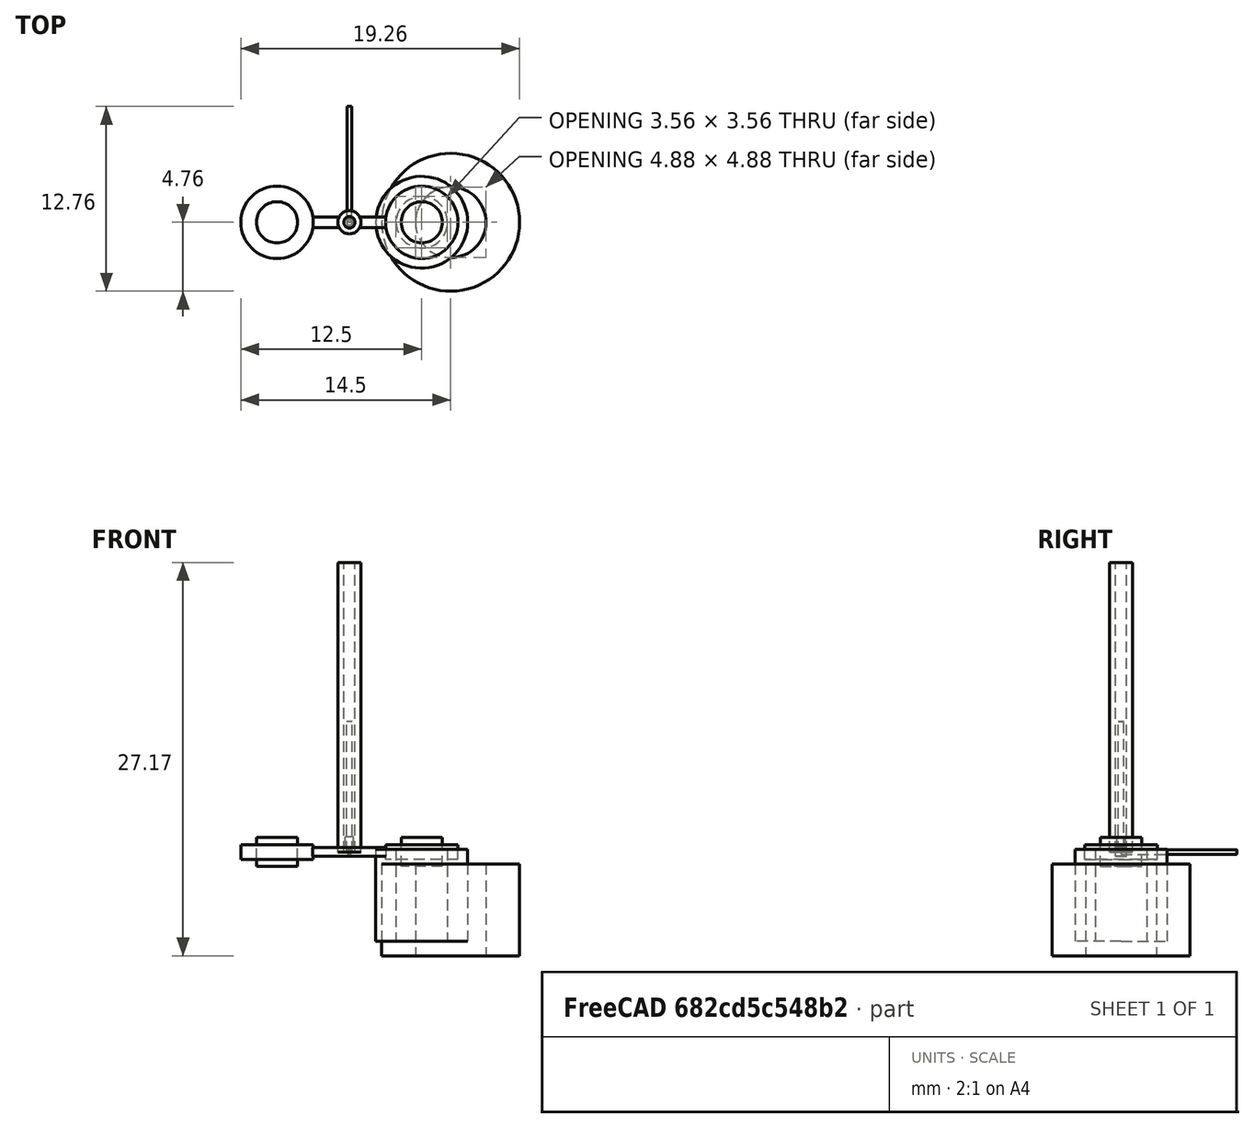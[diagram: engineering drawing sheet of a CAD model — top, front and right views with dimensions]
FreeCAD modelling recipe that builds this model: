
FCSTD DOCUMENT  (FreeCAD 0.18R15536 (Git))
Label: bowtie_5
License: All rights reserved
LicenseURL: http://en.wikipedia.org/wiki/All_rights_reserved
objects: Part::Cylinder×9, Part::MultiFuse×2, Part::Feature×2, Part::Box×1, Spreadsheet::Sheet×1
note: 14 computed .brp shape members not serialized (recipe doc carries the construction recipe); baked Part::Feature solids carry a one-line shape summary decoded from their .brp

FEATURE [Part::Cylinder] Cylinder138  label="BowTieInjectorWire"
  Angle = 360
  AttacherType = Attacher::AttachEngine3D
  Height = 8
  Placement = pos=(0,0,0) rot=(-1,0,0;1.5708rad)
  Radius = 0.165
  expr: Radius = 0.33000000000000002 / 2
FEATURE [Part::Cylinder] Cylinder136  label="BowTieNozzle"
  Angle = 360
  AttacherType = Attacher::AttachEngine3D
  Height = 9
  Radius = 0.2
FEATURE [Part::Cylinder] Cylinder  label="MountingHole1"
  Angle = 360
  AttacherType = Attacher::AttachEngine3D
  Height = 2
  Placement = pos=(-5,0,-1) rot=(0,0,1;0rad)
  Radius = 1.422
  expr: Placement.Base.x = -Sizes.STRIP_LENGTH / 2
  expr: Radius = Sizes.MOUNTING_ID / 2
FEATURE [Part::Box] Box  label="Strip"
  AttacherType = Attacher::AttachEngine3D
  Height = 0.6
  Length = 10
  Placement = pos=(-5,-0.375,-0.3) rot=(0,0,1;0rad)
  Width = 0.75
  expr: Width = Sizes.STRIP_WIDTH
  expr: Placement.Base.y = -Sizes.STRIP_WIDTH / 2
  expr: Length = Sizes.STRIP_LENGTH
  expr: Placement.Base.x = -Sizes.STRIP_LENGTH / 2
  expr: Height = Sizes.STRIP_HEIGHT
  expr: Placement.Base.z = -Sizes.STRIP_HEIGHT / 2
FEATURE [Spreadsheet::Sheet] Spreadsheet  label="Sizes"
  cells = A1=Strip height; B1(STRIP_HEIGHT)=0.59999999999999998; A2=Strip length; B2(STRIP_LENGTH)=10; A3=strip width; B3(STRIP_WIDTH)=0.75; A4=Injection width; B4(INJECTION_WIDTH)=1.5; A5=Injection length; B5(INJECTION_LENGTH)=1.5; A6=Mounting hole ID; B6(MOUNTING_ID)=2.8439999999999999; A7=Nozzle ID; B7(NOZZLE_ID)=0.33000000000000002; A8=Nozzle OD; B8(NOZZLE_OD)=0.59999999999999998; A9=Mounting hole OD; B9(MOUNTING_OD)=5; A10=Nozzle height; B10(NOZZLE_HEIGHT)=0.75; A11=Mounting hole height; B11(MOUNTING_HEIGHT)=1; A12=Ioniz. Col. Length; B12(COL_LENGTH)=20; A13=Ioniz. Col. OD; B13(COL_OD)=1.6000000000000001; A14=Ioniz. Col. ID; B14(COL_ID)=0.78700000000000003; A15=Ioniz. Col. Z
FEATURE [Part::Cylinder] Cylinder139  label="MountingHole2"
  Angle = 360
  AttacherType = Attacher::AttachEngine3D
  Height = 2
  Placement = pos=(5,0,-1) rot=(0,0,1;0rad)
  Radius = 1.422
  expr: Placement.Base.x = Sizes.STRIP_LENGTH / 2
  expr: Radius = Sizes.MOUNTING_ID / 2
FEATURE [Part::Cylinder] Cylinder140  label="Nozzle_OD"
  Angle = 360
  AttacherType = Attacher::AttachEngine3D
  Height = 0.75
  Placement = pos=(0,0,0.3) rot=(0,0,1;0rad)
  Radius = 0.3
  expr: Placement.Base.z = Sizes.STRIP_HEIGHT / 2
  expr: Height = Sizes.NOZZLE_HEIGHT
  expr: Radius = Sizes.NOZZLE_OD / 2
FEATURE [Part::Cylinder] Cylinder141  label="MountingHoleOD"
  Angle = 360
  AttacherType = Attacher::AttachEngine3D
  Height = 1
  Placement = pos=(-5,0,-0.5) rot=(0,0,1;0rad)
  Radius = 2.5
  expr: Radius = Sizes.MOUNTING_OD / 2
  expr: Placement.Base.z = -Sizes.MOUNTING_HEIGHT / 2
  expr: Height = Sizes.MOUNTING_HEIGHT
  expr: Placement.Base.x = -Sizes.STRIP_LENGTH / 2
FEATURE [Part::Cylinder] Cylinder142  label="MountingHoleOD001"
  Angle = 360
  AttacherType = Attacher::AttachEngine3D
  Height = 1
  Placement = pos=(5,0,-0.5) rot=(0,0,1;0rad)
  Radius = 2.5
  expr: Placement.Base.z = -Sizes.MOUNTING_HEIGHT / 2
  expr: Height = Sizes.MOUNTING_HEIGHT
  expr: Placement.Base.x = Sizes.STRIP_LENGTH / 2
  expr: Radius = Sizes.MOUNTING_OD / 2
FEATURE [Part::MultiFuse] Fusion
  Shapes = -> [Box,Cylinder142,Cylinder141,Cylinder140]
FEATURE [Part::MultiFuse] Fusion001
  Shapes = -> [Cylinder138,Cylinder136,Cylinder,Cylinder139]
FEATURE [Part::Cylinder] Cylinder143  label="IonizationColumn"
  Angle = 360
  AttacherType = Attacher::AttachEngine3D
  Height = 20
  Radius = 0.8
  expr: Radius = Sizes.COL_OD / 2
  expr: Height = Sizes.COL_LENGTH
FEATURE [Part::Cylinder] Cylinder144  label="IonizationColumnSubtract"
  Angle = 360
  AttacherType = Attacher::AttachEngine3D
  Height = 20
  Radius = 0.3935
  expr: Radius = Sizes.COL_ID / 2
  expr: Height = Sizes.COL_LENGTH
FEATURE [Part::Feature] Part__Feature  label="96109A160"
  Placement = pos=(5,0,-3) rot=(0,0,1;0rad)
  shape: bbox 6.35 x 6.35 x 6.35 mm, 6 faces (baked)
FEATURE [Part::Feature] Part__Feature001  label="96109A205"
  Placement = pos=(7,0,-4) rot=(0,0,1;0rad)
  shape: bbox 9.525 x 9.525 x 6.35 mm, 6 faces (baked)
